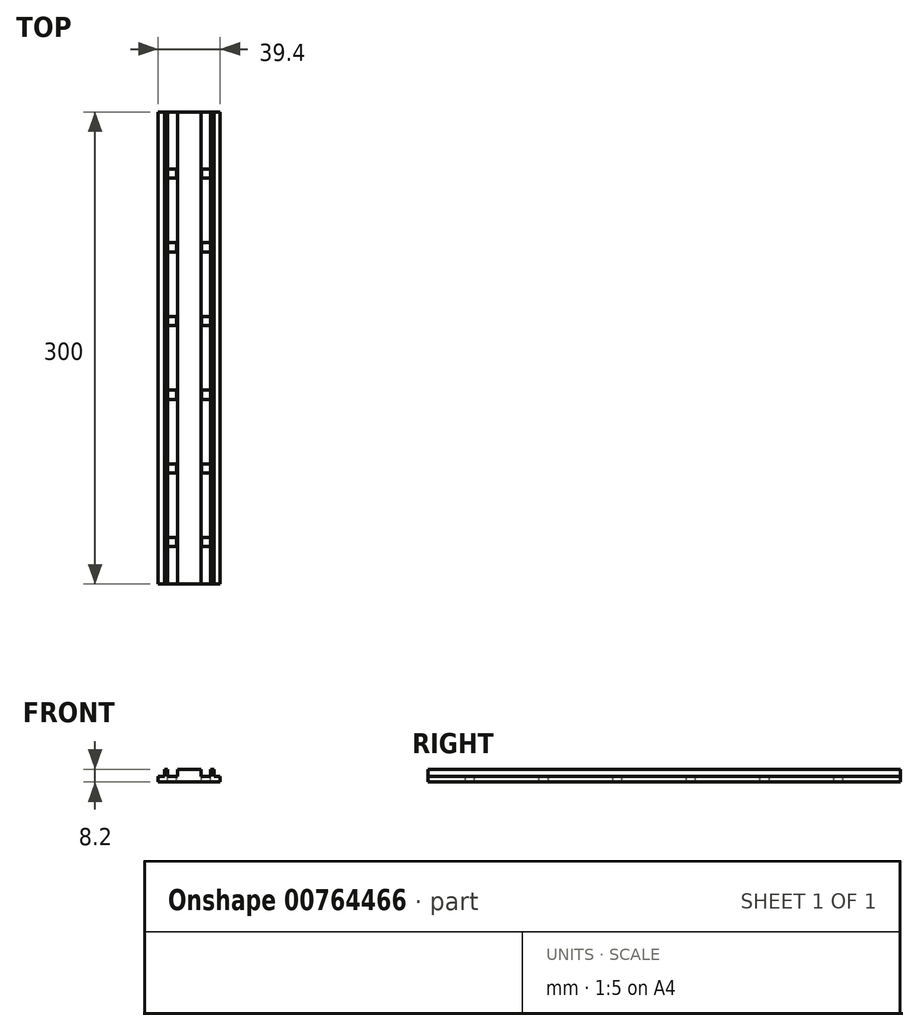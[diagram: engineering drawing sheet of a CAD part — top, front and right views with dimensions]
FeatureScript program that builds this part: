
annotation { "Feature Type Name" : "Feature", "Feature Type Description" : "" }
export const myFeature = defineFeature(function(context is Context, id is Id, definition is map)
    precondition{}
    {
        {
            var Q0;
            Q0=qCreatedBy(makeId("Front.planeOp"),FACE);
            var sketch = newSketch(context, id + "F0", { "sketchPlane" : qUnion([Q0])});
            skLineSegment(sketch, "E0.bottom", {"start": v(-20.15, 0) * mm, "end": v(19.25, 0) * mm});
            skLineSegment(sketch, "E0.top", {"start": v(-20.15, 3.5) * mm, "end": v(-16.15, 3.5) * mm});
            skLineSegment(sketch, "E0.left", {"start": v(-20.15, 0) * mm, "end": v(-20.15, 3.5) * mm});
            skLineSegment(sketch, "E0.right", {"start": v(19.25, 0) * mm, "end": v(19.25, 3.5) * mm});
            skLineSegment(sketch, "E1.top", {"start": v(-16.15, 8.2) * mm, "end": v(-14.15, 8.2) * mm});
            skLineSegment(sketch, "E1.left", {"start": v(-16.15, 3.5) * mm, "end": v(-16.15, 8.2) * mm});
            skLineSegment(sketch, "E1.right", {"start": v(-14.15, 3.5) * mm, "end": v(-14.15, 8.2) * mm});
            skLineSegment(sketch, "E2.top", {"start": v(13.25, 8.2) * mm, "end": v(15.25, 8.2) * mm});
            skLineSegment(sketch, "E2.left", {"start": v(13.25, 3.5) * mm, "end": v(13.25, 8.2) * mm});
            skLineSegment(sketch, "E2.right", {"start": v(15.25, 3.5) * mm, "end": v(15.25, 8.2) * mm});
            skLineSegment(sketch, "E3.top", {"start": v(-7.95, 8.2) * mm, "end": v(7.05, 8.2) * mm});
            skLineSegment(sketch, "E3.left", {"start": v(-7.95, 3.5) * mm, "end": v(-7.95, 8.2) * mm});
            skLineSegment(sketch, "E3.right", {"start": v(7.05, 3.5) * mm, "end": v(7.05, 8.2) * mm});
            skLineSegment(sketch, "E4.trimOffspring", {"start": v(-14.15, 3.5) * mm, "end": v(-7.95, 3.5) * mm});
            skLineSegment(sketch, "E5.trimOffspring", {"start": v(7.05, 3.5) * mm, "end": v(13.25, 3.5) * mm});
            skLineSegment(sketch, "E6.trimOffspring", {"start": v(15.25, 3.5) * mm, "end": v(19.25, 3.5) * mm});
            skSolve(sketch);
        }
        {
            var Q0;
            Q0 = qSketchRegion(id + "F0", true);
            extrude(context, id + "F1", {"entities" : qUnion([Q0]), "oppositeDirection" : true, "depth" : 300 * mm, "offsetDistance" : 25 * mm});
        }
        {
            var Q0;
            Q0=makeQuery(id+"F1.opExtrude","SWEPT_FACE",FACE,{"disambiguationData":[OSD([sQuery(id+"F0.wireOp",EDGE,"E4.trimOffspring")])]});
            var sketch = newSketch(context, id + "F2", { "sketchPlane" : qUnion([Q0])});
            skLineSegment(sketch, "E7.bottom", {"start": v(-14.15, 29.66) * mm, "end": v(-8.35, 29.66) * mm});
            skLineSegment(sketch, "E7.top", {"start": v(-14.15, 23.86) * mm, "end": v(-8.35, 23.86) * mm});
            skLineSegment(sketch, "E7.left", {"start": v(-14.15, 29.66) * mm, "end": v(-14.15, 23.86) * mm});
            skLineSegment(sketch, "E7.right", {"start": v(-8.35, 29.66) * mm, "end": v(-8.35, 23.86) * mm});
            skLineSegment(sketch, "E8.0.1.0", {"start": v(-14.15, 70.66) * mm, "end": v(-8.35, 70.66) * mm});
            skLineSegment(sketch, "E8.0.1.1", {"start": v(-8.35, 76.46) * mm, "end": v(-8.35, 70.66) * mm});
            skLineSegment(sketch, "E8.0.1.2", {"start": v(-14.15, 76.46) * mm, "end": v(-8.35, 76.46) * mm});
            skLineSegment(sketch, "E8.0.1.3", {"start": v(-14.15, 76.46) * mm, "end": v(-14.15, 70.66) * mm});
            skLineSegment(sketch, "E8.0.2.0", {"start": v(-14.15, 117.46) * mm, "end": v(-8.35, 117.46) * mm});
            skLineSegment(sketch, "E8.0.2.1", {"start": v(-8.35, 123.26) * mm, "end": v(-8.35, 117.46) * mm});
            skLineSegment(sketch, "E8.0.2.2", {"start": v(-14.15, 123.26) * mm, "end": v(-8.35, 123.26) * mm});
            skLineSegment(sketch, "E8.0.2.3", {"start": v(-14.15, 123.26) * mm, "end": v(-14.15, 117.46) * mm});
            skLineSegment(sketch, "E8.0.3.0", {"start": v(-14.15, 164.26) * mm, "end": v(-8.35, 164.26) * mm});
            skLineSegment(sketch, "E8.0.3.1", {"start": v(-8.35, 170.06) * mm, "end": v(-8.35, 164.26) * mm});
            skLineSegment(sketch, "E8.0.3.2", {"start": v(-14.15, 170.06) * mm, "end": v(-8.35, 170.06) * mm});
            skLineSegment(sketch, "E8.0.3.3", {"start": v(-14.15, 170.06) * mm, "end": v(-14.15, 164.26) * mm});
            skLineSegment(sketch, "E8.0.4.0", {"start": v(-14.15, 211.06) * mm, "end": v(-8.35, 211.06) * mm});
            skLineSegment(sketch, "E8.0.4.1", {"start": v(-8.35, 216.86) * mm, "end": v(-8.35, 211.06) * mm});
            skLineSegment(sketch, "E8.0.4.2", {"start": v(-14.15, 216.86) * mm, "end": v(-8.35, 216.86) * mm});
            skLineSegment(sketch, "E8.0.4.3", {"start": v(-14.15, 216.86) * mm, "end": v(-14.15, 211.06) * mm});
            skLineSegment(sketch, "E8.0.5.0", {"start": v(-14.15, 257.86) * mm, "end": v(-8.35, 257.86) * mm});
            skLineSegment(sketch, "E8.0.5.1", {"start": v(-8.35, 263.66) * mm, "end": v(-8.35, 257.86) * mm});
            skLineSegment(sketch, "E8.0.5.2", {"start": v(-14.15, 263.66) * mm, "end": v(-8.35, 263.66) * mm});
            skLineSegment(sketch, "E8.0.5.3", {"start": v(-14.15, 263.66) * mm, "end": v(-14.15, 257.86) * mm});
            skLineSegment(sketch, "E8.0.6.0", {"start": v(-14.15, 304.66) * mm, "end": v(-8.35, 304.66) * mm});
            skLineSegment(sketch, "E8.0.6.1", {"start": v(-8.35, 310.46) * mm, "end": v(-8.35, 304.66) * mm});
            skLineSegment(sketch, "E8.0.6.2", {"start": v(-14.15, 310.46) * mm, "end": v(-8.35, 310.46) * mm});
            skLineSegment(sketch, "E8.0.6.3", {"start": v(-14.15, 310.46) * mm, "end": v(-14.15, 304.66) * mm});
            skLineSegment(sketch, "E8.0.7.0", {"start": v(-14.15, 351.46) * mm, "end": v(-8.35, 351.46) * mm});
            skLineSegment(sketch, "E8.0.7.1", {"start": v(-8.35, 357.26) * mm, "end": v(-8.35, 351.46) * mm});
            skLineSegment(sketch, "E8.0.7.2", {"start": v(-14.15, 357.26) * mm, "end": v(-8.35, 357.26) * mm});
            skLineSegment(sketch, "E8.0.7.3", {"start": v(-14.15, 357.26) * mm, "end": v(-14.15, 351.46) * mm});
            skLineSegment(sketch, "E8.0.8.0", {"start": v(-14.15, 398.26) * mm, "end": v(-8.35, 398.26) * mm});
            skLineSegment(sketch, "E8.0.8.1", {"start": v(-8.35, 404.06) * mm, "end": v(-8.35, 398.26) * mm});
            skLineSegment(sketch, "E8.0.8.2", {"start": v(-14.15, 404.06) * mm, "end": v(-8.35, 404.06) * mm});
            skLineSegment(sketch, "E8.0.8.3", {"start": v(-14.15, 404.06) * mm, "end": v(-14.15, 398.26) * mm});
            skLineSegment(sketch, "E8.0.9.0", {"start": v(-14.15, 445.06) * mm, "end": v(-8.35, 445.06) * mm});
            skLineSegment(sketch, "E8.0.9.1", {"start": v(-8.35, 450.86) * mm, "end": v(-8.35, 445.06) * mm});
            skLineSegment(sketch, "E8.0.9.2", {"start": v(-14.15, 450.86) * mm, "end": v(-8.35, 450.86) * mm});
            skLineSegment(sketch, "E8.0.9.3", {"start": v(-14.15, 450.86) * mm, "end": v(-14.15, 445.06) * mm});
            skLineSegment(sketch, "E8.0.10.0", {"start": v(-14.15, 491.86) * mm, "end": v(-8.35, 491.86) * mm});
            skLineSegment(sketch, "E8.0.10.1", {"start": v(-8.35, 497.66) * mm, "end": v(-8.35, 491.86) * mm});
            skLineSegment(sketch, "E8.0.10.2", {"start": v(-14.15, 497.66) * mm, "end": v(-8.35, 497.66) * mm});
            skLineSegment(sketch, "E8.0.10.3", {"start": v(-14.15, 497.66) * mm, "end": v(-14.15, 491.86) * mm});
            skLineSegment(sketch, "E8.0.11.0", {"start": v(-14.15, 538.66) * mm, "end": v(-8.35, 538.66) * mm});
            skLineSegment(sketch, "E8.0.11.1", {"start": v(-8.35, 544.46) * mm, "end": v(-8.35, 538.66) * mm});
            skLineSegment(sketch, "E8.0.11.2", {"start": v(-14.15, 544.46) * mm, "end": v(-8.35, 544.46) * mm});
            skLineSegment(sketch, "E8.0.11.3", {"start": v(-14.15, 544.46) * mm, "end": v(-14.15, 538.66) * mm});
            skLineSegment(sketch, "E8.0.12.0", {"start": v(-14.15, 585.46) * mm, "end": v(-8.35, 585.46) * mm});
            skLineSegment(sketch, "E8.0.12.1", {"start": v(-8.35, 591.26) * mm, "end": v(-8.35, 585.46) * mm});
            skLineSegment(sketch, "E8.0.12.2", {"start": v(-14.15, 591.26) * mm, "end": v(-8.35, 591.26) * mm});
            skLineSegment(sketch, "E8.0.12.3", {"start": v(-14.15, 591.26) * mm, "end": v(-14.15, 585.46) * mm});
            skLineSegment(sketch, "E8.0.13.0", {"start": v(-14.15, 632.26) * mm, "end": v(-8.35, 632.26) * mm});
            skLineSegment(sketch, "E8.0.13.1", {"start": v(-8.35, 638.06) * mm, "end": v(-8.35, 632.26) * mm});
            skLineSegment(sketch, "E8.0.13.2", {"start": v(-14.15, 638.06) * mm, "end": v(-8.35, 638.06) * mm});
            skLineSegment(sketch, "E8.0.13.3", {"start": v(-14.15, 638.06) * mm, "end": v(-14.15, 632.26) * mm});
            skLineSegment(sketch, "E8.0.14.0", {"start": v(-14.15, 679.06) * mm, "end": v(-8.35, 679.06) * mm});
            skLineSegment(sketch, "E8.0.14.1", {"start": v(-8.35, 684.86) * mm, "end": v(-8.35, 679.06) * mm});
            skLineSegment(sketch, "E8.0.14.2", {"start": v(-14.15, 684.86) * mm, "end": v(-8.35, 684.86) * mm});
            skLineSegment(sketch, "E8.0.14.3", {"start": v(-14.15, 684.86) * mm, "end": v(-14.15, 679.06) * mm});
            skLineSegment(sketch, "E8.0.15.0", {"start": v(-14.15, 725.86) * mm, "end": v(-8.35, 725.86) * mm});
            skLineSegment(sketch, "E8.0.15.1", {"start": v(-8.35, 731.66) * mm, "end": v(-8.35, 725.86) * mm});
            skLineSegment(sketch, "E8.0.15.2", {"start": v(-14.15, 731.66) * mm, "end": v(-8.35, 731.66) * mm});
            skLineSegment(sketch, "E8.0.15.3", {"start": v(-14.15, 731.66) * mm, "end": v(-14.15, 725.86) * mm});
            skLineSegment(sketch, "E8.0.16.0", {"start": v(-14.15, 772.66) * mm, "end": v(-8.35, 772.66) * mm});
            skLineSegment(sketch, "E8.0.16.1", {"start": v(-8.35, 778.46) * mm, "end": v(-8.35, 772.66) * mm});
            skLineSegment(sketch, "E8.0.16.2", {"start": v(-14.15, 778.46) * mm, "end": v(-8.35, 778.46) * mm});
            skLineSegment(sketch, "E8.0.16.3", {"start": v(-14.15, 778.46) * mm, "end": v(-14.15, 772.66) * mm});
            skLineSegment(sketch, "E8.0.17.0", {"start": v(-14.15, 819.46) * mm, "end": v(-8.35, 819.46) * mm});
            skLineSegment(sketch, "E8.0.17.1", {"start": v(-8.35, 825.26) * mm, "end": v(-8.35, 819.46) * mm});
            skLineSegment(sketch, "E8.0.17.2", {"start": v(-14.15, 825.26) * mm, "end": v(-8.35, 825.26) * mm});
            skLineSegment(sketch, "E8.0.17.3", {"start": v(-14.15, 825.26) * mm, "end": v(-14.15, 819.46) * mm});
            skLineSegment(sketch, "E8.0.18.0", {"start": v(-14.15, 866.26) * mm, "end": v(-8.35, 866.26) * mm});
            skLineSegment(sketch, "E8.0.18.1", {"start": v(-8.35, 872.06) * mm, "end": v(-8.35, 866.26) * mm});
            skLineSegment(sketch, "E8.0.18.2", {"start": v(-14.15, 872.06) * mm, "end": v(-8.35, 872.06) * mm});
            skLineSegment(sketch, "E8.0.18.3", {"start": v(-14.15, 872.06) * mm, "end": v(-14.15, 866.26) * mm});
            skLineSegment(sketch, "E8.0.19.0", {"start": v(-14.15, 913.06) * mm, "end": v(-8.35, 913.06) * mm});
            skLineSegment(sketch, "E8.0.19.1", {"start": v(-8.35, 918.86) * mm, "end": v(-8.35, 913.06) * mm});
            skLineSegment(sketch, "E8.0.19.2", {"start": v(-14.15, 918.86) * mm, "end": v(-8.35, 918.86) * mm});
            skLineSegment(sketch, "E8.0.19.3", {"start": v(-14.15, 918.86) * mm, "end": v(-14.15, 913.06) * mm});
            skLineSegment(sketch, "E8.0.20.0", {"start": v(-14.15, 959.86) * mm, "end": v(-8.35, 959.86) * mm});
            skLineSegment(sketch, "E8.0.20.1", {"start": v(-8.35, 965.66) * mm, "end": v(-8.35, 959.86) * mm});
            skLineSegment(sketch, "E8.0.20.2", {"start": v(-14.15, 965.66) * mm, "end": v(-8.35, 965.66) * mm});
            skLineSegment(sketch, "E8.0.20.3", {"start": v(-14.15, 965.66) * mm, "end": v(-14.15, 959.86) * mm});
            skLineSegment(sketch, "E8.0.21.0", {"start": v(-14.15, 1006.66) * mm, "end": v(-8.35, 1006.66) * mm});
            skLineSegment(sketch, "E8.0.21.1", {"start": v(-8.35, 1012.46) * mm, "end": v(-8.35, 1006.66) * mm});
            skLineSegment(sketch, "E8.0.21.2", {"start": v(-14.15, 1012.46) * mm, "end": v(-8.35, 1012.46) * mm});
            skLineSegment(sketch, "E8.0.21.3", {"start": v(-14.15, 1012.46) * mm, "end": v(-14.15, 1006.66) * mm});
            skLineSegment(sketch, "E8.0.22.0", {"start": v(-14.15, 1053.46) * mm, "end": v(-8.35, 1053.46) * mm});
            skLineSegment(sketch, "E8.0.22.1", {"start": v(-8.35, 1059.26) * mm, "end": v(-8.35, 1053.46) * mm});
            skLineSegment(sketch, "E8.0.22.2", {"start": v(-14.15, 1059.26) * mm, "end": v(-8.35, 1059.26) * mm});
            skLineSegment(sketch, "E8.0.22.3", {"start": v(-14.15, 1059.26) * mm, "end": v(-14.15, 1053.46) * mm});
            skLineSegment(sketch, "E8.0.23.0", {"start": v(-14.15, 1100.26) * mm, "end": v(-8.35, 1100.26) * mm});
            skLineSegment(sketch, "E8.0.23.1", {"start": v(-8.35, 1106.06) * mm, "end": v(-8.35, 1100.26) * mm});
            skLineSegment(sketch, "E8.0.23.2", {"start": v(-14.15, 1106.06) * mm, "end": v(-8.35, 1106.06) * mm});
            skLineSegment(sketch, "E8.0.23.3", {"start": v(-14.15, 1106.06) * mm, "end": v(-14.15, 1100.26) * mm});
            skLineSegment(sketch, "E8.0.24.0", {"start": v(-14.15, 1147.06) * mm, "end": v(-8.35, 1147.06) * mm});
            skLineSegment(sketch, "E8.0.24.1", {"start": v(-8.35, 1152.86) * mm, "end": v(-8.35, 1147.06) * mm});
            skLineSegment(sketch, "E8.0.24.2", {"start": v(-14.15, 1152.86) * mm, "end": v(-8.35, 1152.86) * mm});
            skLineSegment(sketch, "E8.0.24.3", {"start": v(-14.15, 1152.86) * mm, "end": v(-14.15, 1147.06) * mm});
            skLineSegment(sketch, "E8.0.25.0", {"start": v(-14.15, 1193.86) * mm, "end": v(-8.35, 1193.86) * mm});
            skLineSegment(sketch, "E8.0.25.1", {"start": v(-8.35, 1199.66) * mm, "end": v(-8.35, 1193.86) * mm});
            skLineSegment(sketch, "E8.0.25.2", {"start": v(-14.15, 1199.66) * mm, "end": v(-8.35, 1199.66) * mm});
            skLineSegment(sketch, "E8.0.25.3", {"start": v(-14.15, 1199.66) * mm, "end": v(-14.15, 1193.86) * mm});
            skLineSegment(sketch, "E8.0.26.0", {"start": v(-14.15, 1240.66) * mm, "end": v(-8.35, 1240.66) * mm});
            skLineSegment(sketch, "E8.0.26.1", {"start": v(-8.35, 1246.46) * mm, "end": v(-8.35, 1240.66) * mm});
            skLineSegment(sketch, "E8.0.26.2", {"start": v(-14.15, 1246.46) * mm, "end": v(-8.35, 1246.46) * mm});
            skLineSegment(sketch, "E8.0.26.3", {"start": v(-14.15, 1246.46) * mm, "end": v(-14.15, 1240.66) * mm});
            skLineSegment(sketch, "E8.0.27.0", {"start": v(-14.15, 1287.46) * mm, "end": v(-8.35, 1287.46) * mm});
            skLineSegment(sketch, "E8.0.27.1", {"start": v(-8.35, 1293.26) * mm, "end": v(-8.35, 1287.46) * mm});
            skLineSegment(sketch, "E8.0.27.2", {"start": v(-14.15, 1293.26) * mm, "end": v(-8.35, 1293.26) * mm});
            skLineSegment(sketch, "E8.0.27.3", {"start": v(-14.15, 1293.26) * mm, "end": v(-14.15, 1287.46) * mm});
            skLineSegment(sketch, "E8.0.28.0", {"start": v(-14.15, 1334.26) * mm, "end": v(-8.35, 1334.26) * mm});
            skLineSegment(sketch, "E8.0.28.1", {"start": v(-8.35, 1340.06) * mm, "end": v(-8.35, 1334.26) * mm});
            skLineSegment(sketch, "E8.0.28.2", {"start": v(-14.15, 1340.06) * mm, "end": v(-8.35, 1340.06) * mm});
            skLineSegment(sketch, "E8.0.28.3", {"start": v(-14.15, 1340.06) * mm, "end": v(-14.15, 1334.26) * mm});
            skLineSegment(sketch, "E8.0.29.0", {"start": v(-14.15, 1381.06) * mm, "end": v(-8.35, 1381.06) * mm});
            skLineSegment(sketch, "E8.0.29.1", {"start": v(-8.35, 1386.86) * mm, "end": v(-8.35, 1381.06) * mm});
            skLineSegment(sketch, "E8.0.29.2", {"start": v(-14.15, 1386.86) * mm, "end": v(-8.35, 1386.86) * mm});
            skLineSegment(sketch, "E8.0.29.3", {"start": v(-14.15, 1386.86) * mm, "end": v(-14.15, 1381.06) * mm});
            skLineSegment(sketch, "E8.1.0.0", {"start": v(7.45, 23.86) * mm, "end": v(13.25, 23.86) * mm});
            skLineSegment(sketch, "E8.1.0.1", {"start": v(13.25, 29.66) * mm, "end": v(13.25, 23.86) * mm});
            skLineSegment(sketch, "E8.1.0.2", {"start": v(7.45, 29.66) * mm, "end": v(13.25, 29.66) * mm});
            skLineSegment(sketch, "E8.1.0.3", {"start": v(7.45, 29.66) * mm, "end": v(7.45, 23.86) * mm});
            skLineSegment(sketch, "E8.1.1.0", {"start": v(7.45, 70.66) * mm, "end": v(13.25, 70.66) * mm});
            skLineSegment(sketch, "E8.1.1.1", {"start": v(13.25, 76.46) * mm, "end": v(13.25, 70.66) * mm});
            skLineSegment(sketch, "E8.1.1.2", {"start": v(7.45, 76.46) * mm, "end": v(13.25, 76.46) * mm});
            skLineSegment(sketch, "E8.1.1.3", {"start": v(7.45, 76.46) * mm, "end": v(7.45, 70.66) * mm});
            skLineSegment(sketch, "E8.1.2.0", {"start": v(7.45, 117.46) * mm, "end": v(13.25, 117.46) * mm});
            skLineSegment(sketch, "E8.1.2.1", {"start": v(13.25, 123.26) * mm, "end": v(13.25, 117.46) * mm});
            skLineSegment(sketch, "E8.1.2.2", {"start": v(7.45, 123.26) * mm, "end": v(13.25, 123.26) * mm});
            skLineSegment(sketch, "E8.1.2.3", {"start": v(7.45, 123.26) * mm, "end": v(7.45, 117.46) * mm});
            skLineSegment(sketch, "E8.1.3.0", {"start": v(7.45, 164.26) * mm, "end": v(13.25, 164.26) * mm});
            skLineSegment(sketch, "E8.1.3.1", {"start": v(13.25, 170.06) * mm, "end": v(13.25, 164.26) * mm});
            skLineSegment(sketch, "E8.1.3.2", {"start": v(7.45, 170.06) * mm, "end": v(13.25, 170.06) * mm});
            skLineSegment(sketch, "E8.1.3.3", {"start": v(7.45, 170.06) * mm, "end": v(7.45, 164.26) * mm});
            skLineSegment(sketch, "E8.1.4.0", {"start": v(7.45, 211.06) * mm, "end": v(13.25, 211.06) * mm});
            skLineSegment(sketch, "E8.1.4.1", {"start": v(13.25, 216.86) * mm, "end": v(13.25, 211.06) * mm});
            skLineSegment(sketch, "E8.1.4.2", {"start": v(7.45, 216.86) * mm, "end": v(13.25, 216.86) * mm});
            skLineSegment(sketch, "E8.1.4.3", {"start": v(7.45, 216.86) * mm, "end": v(7.45, 211.06) * mm});
            skLineSegment(sketch, "E8.1.5.0", {"start": v(7.45, 257.86) * mm, "end": v(13.25, 257.86) * mm});
            skLineSegment(sketch, "E8.1.5.1", {"start": v(13.25, 263.66) * mm, "end": v(13.25, 257.86) * mm});
            skLineSegment(sketch, "E8.1.5.2", {"start": v(7.45, 263.66) * mm, "end": v(13.25, 263.66) * mm});
            skLineSegment(sketch, "E8.1.5.3", {"start": v(7.45, 263.66) * mm, "end": v(7.45, 257.86) * mm});
            skLineSegment(sketch, "E8.1.6.0", {"start": v(7.45, 304.66) * mm, "end": v(13.25, 304.66) * mm});
            skLineSegment(sketch, "E8.1.6.1", {"start": v(13.25, 310.46) * mm, "end": v(13.25, 304.66) * mm});
            skLineSegment(sketch, "E8.1.6.2", {"start": v(7.45, 310.46) * mm, "end": v(13.25, 310.46) * mm});
            skLineSegment(sketch, "E8.1.6.3", {"start": v(7.45, 310.46) * mm, "end": v(7.45, 304.66) * mm});
            skLineSegment(sketch, "E8.1.7.0", {"start": v(7.45, 351.46) * mm, "end": v(13.25, 351.46) * mm});
            skLineSegment(sketch, "E8.1.7.1", {"start": v(13.25, 357.26) * mm, "end": v(13.25, 351.46) * mm});
            skLineSegment(sketch, "E8.1.7.2", {"start": v(7.45, 357.26) * mm, "end": v(13.25, 357.26) * mm});
            skLineSegment(sketch, "E8.1.7.3", {"start": v(7.45, 357.26) * mm, "end": v(7.45, 351.46) * mm});
            skLineSegment(sketch, "E8.1.8.0", {"start": v(7.45, 398.26) * mm, "end": v(13.25, 398.26) * mm});
            skLineSegment(sketch, "E8.1.8.1", {"start": v(13.25, 404.06) * mm, "end": v(13.25, 398.26) * mm});
            skLineSegment(sketch, "E8.1.8.2", {"start": v(7.45, 404.06) * mm, "end": v(13.25, 404.06) * mm});
            skLineSegment(sketch, "E8.1.8.3", {"start": v(7.45, 404.06) * mm, "end": v(7.45, 398.26) * mm});
            skLineSegment(sketch, "E8.1.9.0", {"start": v(7.45, 445.06) * mm, "end": v(13.25, 445.06) * mm});
            skLineSegment(sketch, "E8.1.9.1", {"start": v(13.25, 450.86) * mm, "end": v(13.25, 445.06) * mm});
            skLineSegment(sketch, "E8.1.9.2", {"start": v(7.45, 450.86) * mm, "end": v(13.25, 450.86) * mm});
            skLineSegment(sketch, "E8.1.9.3", {"start": v(7.45, 450.86) * mm, "end": v(7.45, 445.06) * mm});
            skLineSegment(sketch, "E8.1.10.0", {"start": v(7.45, 491.86) * mm, "end": v(13.25, 491.86) * mm});
            skLineSegment(sketch, "E8.1.10.1", {"start": v(13.25, 497.66) * mm, "end": v(13.25, 491.86) * mm});
            skLineSegment(sketch, "E8.1.10.2", {"start": v(7.45, 497.66) * mm, "end": v(13.25, 497.66) * mm});
            skLineSegment(sketch, "E8.1.10.3", {"start": v(7.45, 497.66) * mm, "end": v(7.45, 491.86) * mm});
            skLineSegment(sketch, "E8.1.11.0", {"start": v(7.45, 538.66) * mm, "end": v(13.25, 538.66) * mm});
            skLineSegment(sketch, "E8.1.11.1", {"start": v(13.25, 544.46) * mm, "end": v(13.25, 538.66) * mm});
            skLineSegment(sketch, "E8.1.11.2", {"start": v(7.45, 544.46) * mm, "end": v(13.25, 544.46) * mm});
            skLineSegment(sketch, "E8.1.11.3", {"start": v(7.45, 544.46) * mm, "end": v(7.45, 538.66) * mm});
            skLineSegment(sketch, "E8.1.12.0", {"start": v(7.45, 585.46) * mm, "end": v(13.25, 585.46) * mm});
            skLineSegment(sketch, "E8.1.12.1", {"start": v(13.25, 591.26) * mm, "end": v(13.25, 585.46) * mm});
            skLineSegment(sketch, "E8.1.12.2", {"start": v(7.45, 591.26) * mm, "end": v(13.25, 591.26) * mm});
            skLineSegment(sketch, "E8.1.12.3", {"start": v(7.45, 591.26) * mm, "end": v(7.45, 585.46) * mm});
            skLineSegment(sketch, "E8.1.13.0", {"start": v(7.45, 632.26) * mm, "end": v(13.25, 632.26) * mm});
            skLineSegment(sketch, "E8.1.13.1", {"start": v(13.25, 638.06) * mm, "end": v(13.25, 632.26) * mm});
            skLineSegment(sketch, "E8.1.13.2", {"start": v(7.45, 638.06) * mm, "end": v(13.25, 638.06) * mm});
            skLineSegment(sketch, "E8.1.13.3", {"start": v(7.45, 638.06) * mm, "end": v(7.45, 632.26) * mm});
            skLineSegment(sketch, "E8.1.14.0", {"start": v(7.45, 679.06) * mm, "end": v(13.25, 679.06) * mm});
            skLineSegment(sketch, "E8.1.14.1", {"start": v(13.25, 684.86) * mm, "end": v(13.25, 679.06) * mm});
            skLineSegment(sketch, "E8.1.14.2", {"start": v(7.45, 684.86) * mm, "end": v(13.25, 684.86) * mm});
            skLineSegment(sketch, "E8.1.14.3", {"start": v(7.45, 684.86) * mm, "end": v(7.45, 679.06) * mm});
            skLineSegment(sketch, "E8.1.15.0", {"start": v(7.45, 725.86) * mm, "end": v(13.25, 725.86) * mm});
            skLineSegment(sketch, "E8.1.15.1", {"start": v(13.25, 731.66) * mm, "end": v(13.25, 725.86) * mm});
            skLineSegment(sketch, "E8.1.15.2", {"start": v(7.45, 731.66) * mm, "end": v(13.25, 731.66) * mm});
            skLineSegment(sketch, "E8.1.15.3", {"start": v(7.45, 731.66) * mm, "end": v(7.45, 725.86) * mm});
            skLineSegment(sketch, "E8.1.16.0", {"start": v(7.45, 772.66) * mm, "end": v(13.25, 772.66) * mm});
            skLineSegment(sketch, "E8.1.16.1", {"start": v(13.25, 778.46) * mm, "end": v(13.25, 772.66) * mm});
            skLineSegment(sketch, "E8.1.16.2", {"start": v(7.45, 778.46) * mm, "end": v(13.25, 778.46) * mm});
            skLineSegment(sketch, "E8.1.16.3", {"start": v(7.45, 778.46) * mm, "end": v(7.45, 772.66) * mm});
            skLineSegment(sketch, "E8.1.17.0", {"start": v(7.45, 819.46) * mm, "end": v(13.25, 819.46) * mm});
            skLineSegment(sketch, "E8.1.17.1", {"start": v(13.25, 825.26) * mm, "end": v(13.25, 819.46) * mm});
            skLineSegment(sketch, "E8.1.17.2", {"start": v(7.45, 825.26) * mm, "end": v(13.25, 825.26) * mm});
            skLineSegment(sketch, "E8.1.17.3", {"start": v(7.45, 825.26) * mm, "end": v(7.45, 819.46) * mm});
            skLineSegment(sketch, "E8.1.18.0", {"start": v(7.45, 866.26) * mm, "end": v(13.25, 866.26) * mm});
            skLineSegment(sketch, "E8.1.18.1", {"start": v(13.25, 872.06) * mm, "end": v(13.25, 866.26) * mm});
            skLineSegment(sketch, "E8.1.18.2", {"start": v(7.45, 872.06) * mm, "end": v(13.25, 872.06) * mm});
            skLineSegment(sketch, "E8.1.18.3", {"start": v(7.45, 872.06) * mm, "end": v(7.45, 866.26) * mm});
            skLineSegment(sketch, "E8.1.19.0", {"start": v(7.45, 913.06) * mm, "end": v(13.25, 913.06) * mm});
            skLineSegment(sketch, "E8.1.19.1", {"start": v(13.25, 918.86) * mm, "end": v(13.25, 913.06) * mm});
            skLineSegment(sketch, "E8.1.19.2", {"start": v(7.45, 918.86) * mm, "end": v(13.25, 918.86) * mm});
            skLineSegment(sketch, "E8.1.19.3", {"start": v(7.45, 918.86) * mm, "end": v(7.45, 913.06) * mm});
            skLineSegment(sketch, "E8.1.20.0", {"start": v(7.45, 959.86) * mm, "end": v(13.25, 959.86) * mm});
            skLineSegment(sketch, "E8.1.20.1", {"start": v(13.25, 965.66) * mm, "end": v(13.25, 959.86) * mm});
            skLineSegment(sketch, "E8.1.20.2", {"start": v(7.45, 965.66) * mm, "end": v(13.25, 965.66) * mm});
            skLineSegment(sketch, "E8.1.20.3", {"start": v(7.45, 965.66) * mm, "end": v(7.45, 959.86) * mm});
            skLineSegment(sketch, "E8.1.21.0", {"start": v(7.45, 1006.66) * mm, "end": v(13.25, 1006.66) * mm});
            skLineSegment(sketch, "E8.1.21.1", {"start": v(13.25, 1012.46) * mm, "end": v(13.25, 1006.66) * mm});
            skLineSegment(sketch, "E8.1.21.2", {"start": v(7.45, 1012.46) * mm, "end": v(13.25, 1012.46) * mm});
            skLineSegment(sketch, "E8.1.21.3", {"start": v(7.45, 1012.46) * mm, "end": v(7.45, 1006.66) * mm});
            skLineSegment(sketch, "E8.1.22.0", {"start": v(7.45, 1053.46) * mm, "end": v(13.25, 1053.46) * mm});
            skLineSegment(sketch, "E8.1.22.1", {"start": v(13.25, 1059.26) * mm, "end": v(13.25, 1053.46) * mm});
            skLineSegment(sketch, "E8.1.22.2", {"start": v(7.45, 1059.26) * mm, "end": v(13.25, 1059.26) * mm});
            skLineSegment(sketch, "E8.1.22.3", {"start": v(7.45, 1059.26) * mm, "end": v(7.45, 1053.46) * mm});
            skLineSegment(sketch, "E8.1.23.0", {"start": v(7.45, 1100.26) * mm, "end": v(13.25, 1100.26) * mm});
            skLineSegment(sketch, "E8.1.23.1", {"start": v(13.25, 1106.06) * mm, "end": v(13.25, 1100.26) * mm});
            skLineSegment(sketch, "E8.1.23.2", {"start": v(7.45, 1106.06) * mm, "end": v(13.25, 1106.06) * mm});
            skLineSegment(sketch, "E8.1.23.3", {"start": v(7.45, 1106.06) * mm, "end": v(7.45, 1100.26) * mm});
            skLineSegment(sketch, "E8.1.24.0", {"start": v(7.45, 1147.06) * mm, "end": v(13.25, 1147.06) * mm});
            skLineSegment(sketch, "E8.1.24.1", {"start": v(13.25, 1152.86) * mm, "end": v(13.25, 1147.06) * mm});
            skLineSegment(sketch, "E8.1.24.2", {"start": v(7.45, 1152.86) * mm, "end": v(13.25, 1152.86) * mm});
            skLineSegment(sketch, "E8.1.24.3", {"start": v(7.45, 1152.86) * mm, "end": v(7.45, 1147.06) * mm});
            skLineSegment(sketch, "E8.1.25.0", {"start": v(7.45, 1193.86) * mm, "end": v(13.25, 1193.86) * mm});
            skLineSegment(sketch, "E8.1.25.1", {"start": v(13.25, 1199.66) * mm, "end": v(13.25, 1193.86) * mm});
            skLineSegment(sketch, "E8.1.25.2", {"start": v(7.45, 1199.66) * mm, "end": v(13.25, 1199.66) * mm});
            skLineSegment(sketch, "E8.1.25.3", {"start": v(7.45, 1199.66) * mm, "end": v(7.45, 1193.86) * mm});
            skLineSegment(sketch, "E8.1.26.0", {"start": v(7.45, 1240.66) * mm, "end": v(13.25, 1240.66) * mm});
            skLineSegment(sketch, "E8.1.26.1", {"start": v(13.25, 1246.46) * mm, "end": v(13.25, 1240.66) * mm});
            skLineSegment(sketch, "E8.1.26.2", {"start": v(7.45, 1246.46) * mm, "end": v(13.25, 1246.46) * mm});
            skLineSegment(sketch, "E8.1.26.3", {"start": v(7.45, 1246.46) * mm, "end": v(7.45, 1240.66) * mm});
            skLineSegment(sketch, "E8.1.27.0", {"start": v(7.45, 1287.46) * mm, "end": v(13.25, 1287.46) * mm});
            skLineSegment(sketch, "E8.1.27.1", {"start": v(13.25, 1293.26) * mm, "end": v(13.25, 1287.46) * mm});
            skLineSegment(sketch, "E8.1.27.2", {"start": v(7.45, 1293.26) * mm, "end": v(13.25, 1293.26) * mm});
            skLineSegment(sketch, "E8.1.27.3", {"start": v(7.45, 1293.26) * mm, "end": v(7.45, 1287.46) * mm});
            skLineSegment(sketch, "E8.1.28.0", {"start": v(7.45, 1334.26) * mm, "end": v(13.25, 1334.26) * mm});
            skLineSegment(sketch, "E8.1.28.1", {"start": v(13.25, 1340.06) * mm, "end": v(13.25, 1334.26) * mm});
            skLineSegment(sketch, "E8.1.28.2", {"start": v(7.45, 1340.06) * mm, "end": v(13.25, 1340.06) * mm});
            skLineSegment(sketch, "E8.1.28.3", {"start": v(7.45, 1340.06) * mm, "end": v(7.45, 1334.26) * mm});
            skLineSegment(sketch, "E8.1.29.0", {"start": v(7.45, 1381.06) * mm, "end": v(13.25, 1381.06) * mm});
            skLineSegment(sketch, "E8.1.29.1", {"start": v(13.25, 1386.86) * mm, "end": v(13.25, 1381.06) * mm});
            skLineSegment(sketch, "E8.1.29.2", {"start": v(7.45, 1386.86) * mm, "end": v(13.25, 1386.86) * mm});
            skLineSegment(sketch, "E8.1.29.3", {"start": v(7.45, 1386.86) * mm, "end": v(7.45, 1381.06) * mm});
            skLineSegment(sketch, "E8.direction1", {"start": v(-14.15, 23.86) * mm, "end": v(7.45, 23.86) * mm, "construction": true});
            skLineSegment(sketch, "E8.direction2", {"start": v(-14.15, 23.86) * mm, "end": v(-14.15, 70.66) * mm, "construction": true});
            skLineSegment(sketch, "E9.0.0.30", {"start": v(-14.15, 1427.86) * mm, "end": v(-8.35, 1427.86) * mm});
            skLineSegment(sketch, "E9.3.0.30", {"start": v(-8.35, 1433.66) * mm, "end": v(-8.35, 1427.86) * mm});
            skLineSegment(sketch, "E9.6.0.30", {"start": v(-14.15, 1433.66) * mm, "end": v(-8.35, 1433.66) * mm});
            skLineSegment(sketch, "E9.9.0.30", {"start": v(-14.15, 1433.66) * mm, "end": v(-14.15, 1427.86) * mm});
            skLineSegment(sketch, "E9.0.0.31", {"start": v(-14.15, 1474.66) * mm, "end": v(-8.35, 1474.66) * mm});
            skLineSegment(sketch, "E9.3.0.31", {"start": v(-8.35, 1480.46) * mm, "end": v(-8.35, 1474.66) * mm});
            skLineSegment(sketch, "E9.6.0.31", {"start": v(-14.15, 1480.46) * mm, "end": v(-8.35, 1480.46) * mm});
            skLineSegment(sketch, "E9.9.0.31", {"start": v(-14.15, 1480.46) * mm, "end": v(-14.15, 1474.66) * mm});
            skLineSegment(sketch, "E9.0.0.32", {"start": v(-14.15, 1521.46) * mm, "end": v(-8.35, 1521.46) * mm});
            skLineSegment(sketch, "E9.3.0.32", {"start": v(-8.35, 1527.26) * mm, "end": v(-8.35, 1521.46) * mm});
            skLineSegment(sketch, "E9.6.0.32", {"start": v(-14.15, 1527.26) * mm, "end": v(-8.35, 1527.26) * mm});
            skLineSegment(sketch, "E9.9.0.32", {"start": v(-14.15, 1527.26) * mm, "end": v(-14.15, 1521.46) * mm});
            skLineSegment(sketch, "E9.0.0.33", {"start": v(-14.15, 1568.26) * mm, "end": v(-8.35, 1568.26) * mm});
            skLineSegment(sketch, "E9.3.0.33", {"start": v(-8.35, 1574.06) * mm, "end": v(-8.35, 1568.26) * mm});
            skLineSegment(sketch, "E9.6.0.33", {"start": v(-14.15, 1574.06) * mm, "end": v(-8.35, 1574.06) * mm});
            skLineSegment(sketch, "E9.9.0.33", {"start": v(-14.15, 1574.06) * mm, "end": v(-14.15, 1568.26) * mm});
            skLineSegment(sketch, "E9.0.0.34", {"start": v(-14.15, 1615.06) * mm, "end": v(-8.35, 1615.06) * mm});
            skLineSegment(sketch, "E9.3.0.34", {"start": v(-8.35, 1620.86) * mm, "end": v(-8.35, 1615.06) * mm});
            skLineSegment(sketch, "E9.6.0.34", {"start": v(-14.15, 1620.86) * mm, "end": v(-8.35, 1620.86) * mm});
            skLineSegment(sketch, "E9.9.0.34", {"start": v(-14.15, 1620.86) * mm, "end": v(-14.15, 1615.06) * mm});
            skLineSegment(sketch, "E9.0.0.35", {"start": v(-14.15, 1661.86) * mm, "end": v(-8.35, 1661.86) * mm});
            skLineSegment(sketch, "E9.3.0.35", {"start": v(-8.35, 1667.66) * mm, "end": v(-8.35, 1661.86) * mm});
            skLineSegment(sketch, "E9.6.0.35", {"start": v(-14.15, 1667.66) * mm, "end": v(-8.35, 1667.66) * mm});
            skLineSegment(sketch, "E9.9.0.35", {"start": v(-14.15, 1667.66) * mm, "end": v(-14.15, 1661.86) * mm});
            skLineSegment(sketch, "E9.0.0.36", {"start": v(-14.15, 1708.66) * mm, "end": v(-8.35, 1708.66) * mm});
            skLineSegment(sketch, "E9.3.0.36", {"start": v(-8.35, 1714.46) * mm, "end": v(-8.35, 1708.66) * mm});
            skLineSegment(sketch, "E9.6.0.36", {"start": v(-14.15, 1714.46) * mm, "end": v(-8.35, 1714.46) * mm});
            skLineSegment(sketch, "E9.9.0.36", {"start": v(-14.15, 1714.46) * mm, "end": v(-14.15, 1708.66) * mm});
            skLineSegment(sketch, "E9.0.0.37", {"start": v(-14.15, 1755.46) * mm, "end": v(-8.35, 1755.46) * mm});
            skLineSegment(sketch, "E9.3.0.37", {"start": v(-8.35, 1761.26) * mm, "end": v(-8.35, 1755.46) * mm});
            skLineSegment(sketch, "E9.6.0.37", {"start": v(-14.15, 1761.26) * mm, "end": v(-8.35, 1761.26) * mm});
            skLineSegment(sketch, "E9.9.0.37", {"start": v(-14.15, 1761.26) * mm, "end": v(-14.15, 1755.46) * mm});
            skLineSegment(sketch, "E9.0.0.38", {"start": v(-14.15, 1802.26) * mm, "end": v(-8.35, 1802.26) * mm});
            skLineSegment(sketch, "E9.3.0.38", {"start": v(-8.35, 1808.06) * mm, "end": v(-8.35, 1802.26) * mm});
            skLineSegment(sketch, "E9.6.0.38", {"start": v(-14.15, 1808.06) * mm, "end": v(-8.35, 1808.06) * mm});
            skLineSegment(sketch, "E9.9.0.38", {"start": v(-14.15, 1808.06) * mm, "end": v(-14.15, 1802.26) * mm});
            skLineSegment(sketch, "E9.0.0.39", {"start": v(-14.15, 1849.06) * mm, "end": v(-8.35, 1849.06) * mm});
            skLineSegment(sketch, "E9.3.0.39", {"start": v(-8.35, 1854.86) * mm, "end": v(-8.35, 1849.06) * mm});
            skLineSegment(sketch, "E9.6.0.39", {"start": v(-14.15, 1854.86) * mm, "end": v(-8.35, 1854.86) * mm});
            skLineSegment(sketch, "E9.9.0.39", {"start": v(-14.15, 1854.86) * mm, "end": v(-14.15, 1849.06) * mm});
            skLineSegment(sketch, "E9.0.0.40", {"start": v(-14.15, 1895.86) * mm, "end": v(-8.35, 1895.86) * mm});
            skLineSegment(sketch, "E9.3.0.40", {"start": v(-8.35, 1901.66) * mm, "end": v(-8.35, 1895.86) * mm});
            skLineSegment(sketch, "E9.6.0.40", {"start": v(-14.15, 1901.66) * mm, "end": v(-8.35, 1901.66) * mm});
            skLineSegment(sketch, "E9.9.0.40", {"start": v(-14.15, 1901.66) * mm, "end": v(-14.15, 1895.86) * mm});
            skLineSegment(sketch, "E9.0.0.41", {"start": v(-14.15, 1942.66) * mm, "end": v(-8.35, 1942.66) * mm});
            skLineSegment(sketch, "E9.3.0.41", {"start": v(-8.35, 1948.46) * mm, "end": v(-8.35, 1942.66) * mm});
            skLineSegment(sketch, "E9.6.0.41", {"start": v(-14.15, 1948.46) * mm, "end": v(-8.35, 1948.46) * mm});
            skLineSegment(sketch, "E9.9.0.41", {"start": v(-14.15, 1948.46) * mm, "end": v(-14.15, 1942.66) * mm});
            skLineSegment(sketch, "E9.0.0.42", {"start": v(-14.15, 1989.46) * mm, "end": v(-8.35, 1989.46) * mm});
            skLineSegment(sketch, "E9.3.0.42", {"start": v(-8.35, 1995.26) * mm, "end": v(-8.35, 1989.46) * mm});
            skLineSegment(sketch, "E9.6.0.42", {"start": v(-14.15, 1995.26) * mm, "end": v(-8.35, 1995.26) * mm});
            skLineSegment(sketch, "E9.9.0.42", {"start": v(-14.15, 1995.26) * mm, "end": v(-14.15, 1989.46) * mm});
            skLineSegment(sketch, "E9.0.0.43", {"start": v(-14.15, 2036.26) * mm, "end": v(-8.35, 2036.26) * mm});
            skLineSegment(sketch, "E9.3.0.43", {"start": v(-8.35, 2042.06) * mm, "end": v(-8.35, 2036.26) * mm});
            skLineSegment(sketch, "E9.6.0.43", {"start": v(-14.15, 2042.06) * mm, "end": v(-8.35, 2042.06) * mm});
            skLineSegment(sketch, "E9.9.0.43", {"start": v(-14.15, 2042.06) * mm, "end": v(-14.15, 2036.26) * mm});
            skLineSegment(sketch, "E9.0.0.44", {"start": v(-14.15, 2083.06) * mm, "end": v(-8.35, 2083.06) * mm});
            skLineSegment(sketch, "E9.3.0.44", {"start": v(-8.35, 2088.86) * mm, "end": v(-8.35, 2083.06) * mm});
            skLineSegment(sketch, "E9.6.0.44", {"start": v(-14.15, 2088.86) * mm, "end": v(-8.35, 2088.86) * mm});
            skLineSegment(sketch, "E9.9.0.44", {"start": v(-14.15, 2088.86) * mm, "end": v(-14.15, 2083.06) * mm});
            skLineSegment(sketch, "E9.0.0.45", {"start": v(-14.15, 2129.86) * mm, "end": v(-8.35, 2129.86) * mm});
            skLineSegment(sketch, "E9.3.0.45", {"start": v(-8.35, 2135.66) * mm, "end": v(-8.35, 2129.86) * mm});
            skLineSegment(sketch, "E9.6.0.45", {"start": v(-14.15, 2135.66) * mm, "end": v(-8.35, 2135.66) * mm});
            skLineSegment(sketch, "E9.9.0.45", {"start": v(-14.15, 2135.66) * mm, "end": v(-14.15, 2129.86) * mm});
            skLineSegment(sketch, "E9.0.0.46", {"start": v(-14.15, 2176.66) * mm, "end": v(-8.35, 2176.66) * mm});
            skLineSegment(sketch, "E9.3.0.46", {"start": v(-8.35, 2182.46) * mm, "end": v(-8.35, 2176.66) * mm});
            skLineSegment(sketch, "E9.6.0.46", {"start": v(-14.15, 2182.46) * mm, "end": v(-8.35, 2182.46) * mm});
            skLineSegment(sketch, "E9.9.0.46", {"start": v(-14.15, 2182.46) * mm, "end": v(-14.15, 2176.66) * mm});
            skLineSegment(sketch, "E9.0.0.47", {"start": v(-14.15, 2223.46) * mm, "end": v(-8.35, 2223.46) * mm});
            skLineSegment(sketch, "E9.3.0.47", {"start": v(-8.35, 2229.26) * mm, "end": v(-8.35, 2223.46) * mm});
            skLineSegment(sketch, "E9.6.0.47", {"start": v(-14.15, 2229.26) * mm, "end": v(-8.35, 2229.26) * mm});
            skLineSegment(sketch, "E9.9.0.47", {"start": v(-14.15, 2229.26) * mm, "end": v(-14.15, 2223.46) * mm});
            skLineSegment(sketch, "E9.0.0.48", {"start": v(-14.15, 2270.26) * mm, "end": v(-8.35, 2270.26) * mm});
            skLineSegment(sketch, "E9.3.0.48", {"start": v(-8.35, 2276.06) * mm, "end": v(-8.35, 2270.26) * mm});
            skLineSegment(sketch, "E9.6.0.48", {"start": v(-14.15, 2276.06) * mm, "end": v(-8.35, 2276.06) * mm});
            skLineSegment(sketch, "E9.9.0.48", {"start": v(-14.15, 2276.06) * mm, "end": v(-14.15, 2270.26) * mm});
            skLineSegment(sketch, "E9.0.0.49", {"start": v(-14.15, 2317.06) * mm, "end": v(-8.35, 2317.06) * mm});
            skLineSegment(sketch, "E9.3.0.49", {"start": v(-8.35, 2322.86) * mm, "end": v(-8.35, 2317.06) * mm});
            skLineSegment(sketch, "E9.6.0.49", {"start": v(-14.15, 2322.86) * mm, "end": v(-8.35, 2322.86) * mm});
            skLineSegment(sketch, "E9.9.0.49", {"start": v(-14.15, 2322.86) * mm, "end": v(-14.15, 2317.06) * mm});
            skLineSegment(sketch, "E9.0.1.30", {"start": v(7.45, 1427.86) * mm, "end": v(13.25, 1427.86) * mm});
            skLineSegment(sketch, "E9.3.1.30", {"start": v(13.25, 1433.66) * mm, "end": v(13.25, 1427.86) * mm});
            skLineSegment(sketch, "E9.6.1.30", {"start": v(7.45, 1433.66) * mm, "end": v(13.25, 1433.66) * mm});
            skLineSegment(sketch, "E9.9.1.30", {"start": v(7.45, 1433.66) * mm, "end": v(7.45, 1427.86) * mm});
            skLineSegment(sketch, "E9.0.1.31", {"start": v(7.45, 1474.66) * mm, "end": v(13.25, 1474.66) * mm});
            skLineSegment(sketch, "E9.3.1.31", {"start": v(13.25, 1480.46) * mm, "end": v(13.25, 1474.66) * mm});
            skLineSegment(sketch, "E9.6.1.31", {"start": v(7.45, 1480.46) * mm, "end": v(13.25, 1480.46) * mm});
            skLineSegment(sketch, "E9.9.1.31", {"start": v(7.45, 1480.46) * mm, "end": v(7.45, 1474.66) * mm});
            skLineSegment(sketch, "E9.0.1.32", {"start": v(7.45, 1521.46) * mm, "end": v(13.25, 1521.46) * mm});
            skLineSegment(sketch, "E9.3.1.32", {"start": v(13.25, 1527.26) * mm, "end": v(13.25, 1521.46) * mm});
            skLineSegment(sketch, "E9.6.1.32", {"start": v(7.45, 1527.26) * mm, "end": v(13.25, 1527.26) * mm});
            skLineSegment(sketch, "E9.9.1.32", {"start": v(7.45, 1527.26) * mm, "end": v(7.45, 1521.46) * mm});
            skLineSegment(sketch, "E9.0.1.33", {"start": v(7.45, 1568.26) * mm, "end": v(13.25, 1568.26) * mm});
            skLineSegment(sketch, "E9.3.1.33", {"start": v(13.25, 1574.06) * mm, "end": v(13.25, 1568.26) * mm});
            skLineSegment(sketch, "E9.6.1.33", {"start": v(7.45, 1574.06) * mm, "end": v(13.25, 1574.06) * mm});
            skLineSegment(sketch, "E9.9.1.33", {"start": v(7.45, 1574.06) * mm, "end": v(7.45, 1568.26) * mm});
            skLineSegment(sketch, "E9.0.1.34", {"start": v(7.45, 1615.06) * mm, "end": v(13.25, 1615.06) * mm});
            skLineSegment(sketch, "E9.3.1.34", {"start": v(13.25, 1620.86) * mm, "end": v(13.25, 1615.06) * mm});
            skLineSegment(sketch, "E9.6.1.34", {"start": v(7.45, 1620.86) * mm, "end": v(13.25, 1620.86) * mm});
            skLineSegment(sketch, "E9.9.1.34", {"start": v(7.45, 1620.86) * mm, "end": v(7.45, 1615.06) * mm});
            skLineSegment(sketch, "E9.0.1.35", {"start": v(7.45, 1661.86) * mm, "end": v(13.25, 1661.86) * mm});
            skLineSegment(sketch, "E9.3.1.35", {"start": v(13.25, 1667.66) * mm, "end": v(13.25, 1661.86) * mm});
            skLineSegment(sketch, "E9.6.1.35", {"start": v(7.45, 1667.66) * mm, "end": v(13.25, 1667.66) * mm});
            skLineSegment(sketch, "E9.9.1.35", {"start": v(7.45, 1667.66) * mm, "end": v(7.45, 1661.86) * mm});
            skLineSegment(sketch, "E9.0.1.36", {"start": v(7.45, 1708.66) * mm, "end": v(13.25, 1708.66) * mm});
            skLineSegment(sketch, "E9.3.1.36", {"start": v(13.25, 1714.46) * mm, "end": v(13.25, 1708.66) * mm});
            skLineSegment(sketch, "E9.6.1.36", {"start": v(7.45, 1714.46) * mm, "end": v(13.25, 1714.46) * mm});
            skLineSegment(sketch, "E9.9.1.36", {"start": v(7.45, 1714.46) * mm, "end": v(7.45, 1708.66) * mm});
            skLineSegment(sketch, "E9.0.1.37", {"start": v(7.45, 1755.46) * mm, "end": v(13.25, 1755.46) * mm});
            skLineSegment(sketch, "E9.3.1.37", {"start": v(13.25, 1761.26) * mm, "end": v(13.25, 1755.46) * mm});
            skLineSegment(sketch, "E9.6.1.37", {"start": v(7.45, 1761.26) * mm, "end": v(13.25, 1761.26) * mm});
            skLineSegment(sketch, "E9.9.1.37", {"start": v(7.45, 1761.26) * mm, "end": v(7.45, 1755.46) * mm});
            skLineSegment(sketch, "E9.0.1.38", {"start": v(7.45, 1802.26) * mm, "end": v(13.25, 1802.26) * mm});
            skLineSegment(sketch, "E9.3.1.38", {"start": v(13.25, 1808.06) * mm, "end": v(13.25, 1802.26) * mm});
            skLineSegment(sketch, "E9.6.1.38", {"start": v(7.45, 1808.06) * mm, "end": v(13.25, 1808.06) * mm});
            skLineSegment(sketch, "E9.9.1.38", {"start": v(7.45, 1808.06) * mm, "end": v(7.45, 1802.26) * mm});
            skLineSegment(sketch, "E9.0.1.39", {"start": v(7.45, 1849.06) * mm, "end": v(13.25, 1849.06) * mm});
            skLineSegment(sketch, "E9.3.1.39", {"start": v(13.25, 1854.86) * mm, "end": v(13.25, 1849.06) * mm});
            skLineSegment(sketch, "E9.6.1.39", {"start": v(7.45, 1854.86) * mm, "end": v(13.25, 1854.86) * mm});
            skLineSegment(sketch, "E9.9.1.39", {"start": v(7.45, 1854.86) * mm, "end": v(7.45, 1849.06) * mm});
            skLineSegment(sketch, "E9.0.1.40", {"start": v(7.45, 1895.86) * mm, "end": v(13.25, 1895.86) * mm});
            skLineSegment(sketch, "E9.3.1.40", {"start": v(13.25, 1901.66) * mm, "end": v(13.25, 1895.86) * mm});
            skLineSegment(sketch, "E9.6.1.40", {"start": v(7.45, 1901.66) * mm, "end": v(13.25, 1901.66) * mm});
            skLineSegment(sketch, "E9.9.1.40", {"start": v(7.45, 1901.66) * mm, "end": v(7.45, 1895.86) * mm});
            skLineSegment(sketch, "E9.0.1.41", {"start": v(7.45, 1942.66) * mm, "end": v(13.25, 1942.66) * mm});
            skLineSegment(sketch, "E9.3.1.41", {"start": v(13.25, 1948.46) * mm, "end": v(13.25, 1942.66) * mm});
            skLineSegment(sketch, "E9.6.1.41", {"start": v(7.45, 1948.46) * mm, "end": v(13.25, 1948.46) * mm});
            skLineSegment(sketch, "E9.9.1.41", {"start": v(7.45, 1948.46) * mm, "end": v(7.45, 1942.66) * mm});
            skLineSegment(sketch, "E9.0.1.42", {"start": v(7.45, 1989.46) * mm, "end": v(13.25, 1989.46) * mm});
            skLineSegment(sketch, "E9.3.1.42", {"start": v(13.25, 1995.26) * mm, "end": v(13.25, 1989.46) * mm});
            skLineSegment(sketch, "E9.6.1.42", {"start": v(7.45, 1995.26) * mm, "end": v(13.25, 1995.26) * mm});
            skLineSegment(sketch, "E9.9.1.42", {"start": v(7.45, 1995.26) * mm, "end": v(7.45, 1989.46) * mm});
            skLineSegment(sketch, "E9.0.1.43", {"start": v(7.45, 2036.26) * mm, "end": v(13.25, 2036.26) * mm});
            skLineSegment(sketch, "E9.3.1.43", {"start": v(13.25, 2042.06) * mm, "end": v(13.25, 2036.26) * mm});
            skLineSegment(sketch, "E9.6.1.43", {"start": v(7.45, 2042.06) * mm, "end": v(13.25, 2042.06) * mm});
            skLineSegment(sketch, "E9.9.1.43", {"start": v(7.45, 2042.06) * mm, "end": v(7.45, 2036.26) * mm});
            skLineSegment(sketch, "E9.0.1.44", {"start": v(7.45, 2083.06) * mm, "end": v(13.25, 2083.06) * mm});
            skLineSegment(sketch, "E9.3.1.44", {"start": v(13.25, 2088.86) * mm, "end": v(13.25, 2083.06) * mm});
            skLineSegment(sketch, "E9.6.1.44", {"start": v(7.45, 2088.86) * mm, "end": v(13.25, 2088.86) * mm});
            skLineSegment(sketch, "E9.9.1.44", {"start": v(7.45, 2088.86) * mm, "end": v(7.45, 2083.06) * mm});
            skLineSegment(sketch, "E9.0.1.45", {"start": v(7.45, 2129.86) * mm, "end": v(13.25, 2129.86) * mm});
            skLineSegment(sketch, "E9.3.1.45", {"start": v(13.25, 2135.66) * mm, "end": v(13.25, 2129.86) * mm});
            skLineSegment(sketch, "E9.6.1.45", {"start": v(7.45, 2135.66) * mm, "end": v(13.25, 2135.66) * mm});
            skLineSegment(sketch, "E9.9.1.45", {"start": v(7.45, 2135.66) * mm, "end": v(7.45, 2129.86) * mm});
            skLineSegment(sketch, "E9.0.1.46", {"start": v(7.45, 2176.66) * mm, "end": v(13.25, 2176.66) * mm});
            skLineSegment(sketch, "E9.3.1.46", {"start": v(13.25, 2182.46) * mm, "end": v(13.25, 2176.66) * mm});
            skLineSegment(sketch, "E9.6.1.46", {"start": v(7.45, 2182.46) * mm, "end": v(13.25, 2182.46) * mm});
            skLineSegment(sketch, "E9.9.1.46", {"start": v(7.45, 2182.46) * mm, "end": v(7.45, 2176.66) * mm});
            skLineSegment(sketch, "E9.0.1.47", {"start": v(7.45, 2223.46) * mm, "end": v(13.25, 2223.46) * mm});
            skLineSegment(sketch, "E9.3.1.47", {"start": v(13.25, 2229.26) * mm, "end": v(13.25, 2223.46) * mm});
            skLineSegment(sketch, "E9.6.1.47", {"start": v(7.45, 2229.26) * mm, "end": v(13.25, 2229.26) * mm});
            skLineSegment(sketch, "E9.9.1.47", {"start": v(7.45, 2229.26) * mm, "end": v(7.45, 2223.46) * mm});
            skLineSegment(sketch, "E9.0.1.48", {"start": v(7.45, 2270.26) * mm, "end": v(13.25, 2270.26) * mm});
            skLineSegment(sketch, "E9.3.1.48", {"start": v(13.25, 2276.06) * mm, "end": v(13.25, 2270.26) * mm});
            skLineSegment(sketch, "E9.6.1.48", {"start": v(7.45, 2276.06) * mm, "end": v(13.25, 2276.06) * mm});
            skLineSegment(sketch, "E9.9.1.48", {"start": v(7.45, 2276.06) * mm, "end": v(7.45, 2270.26) * mm});
            skLineSegment(sketch, "E9.0.1.49", {"start": v(7.45, 2317.06) * mm, "end": v(13.25, 2317.06) * mm});
            skLineSegment(sketch, "E9.3.1.49", {"start": v(13.25, 2322.86) * mm, "end": v(13.25, 2317.06) * mm});
            skLineSegment(sketch, "E9.6.1.49", {"start": v(7.45, 2322.86) * mm, "end": v(13.25, 2322.86) * mm});
            skLineSegment(sketch, "E9.9.1.49", {"start": v(7.45, 2322.86) * mm, "end": v(7.45, 2317.06) * mm});
            skSolve(sketch);
        }
        {
            var Q0;
            Q0 = qSketchRegion(id + "F2", true);
            extrude(context, id + "F3", {"entities" : qUnion([Q0]), "operationType" : NewBodyOperationType.REMOVE, "endBound" : BoundingType.THROUGH_ALL, "oppositeDirection" : true, "depth" : 25 * mm, "offsetDistance" : 25 * mm});
        }
    });
